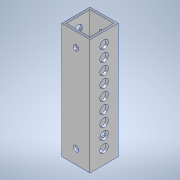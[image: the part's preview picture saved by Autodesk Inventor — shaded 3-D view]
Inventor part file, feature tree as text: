
AUTODESK INVENTOR PART (.ipt)
format: ipt  version: 2020.3 (Build 243373000, 373)  size: 161,280 bytes
history: native  units: mm
features: sketch x3, hole x2, other x1, extrude x1
ambient origin geometry x8: Origin, YZ Plane, XZ Plane, XY Plane, X Axis, Y Axis, Z Axis, Center Point
bodies: Body1 (feature_tree)
feature tree (7):
  other  "ソリッド1"
  extrude  "押し出し1"  Depth=15.0mm
  hole  "穴1"  [1 undecoded]
  hole  "穴2"  [1 undecoded]
  sketch  "スケッチ1"
  sketch  "スケッチ2"
  sketch  "スケッチ3"
note: 2 required parameter values undecoded (feature->parameter linkage not recoverable at this tier; creation-order binding heuristic only, values carry confidence <= 0.55)
